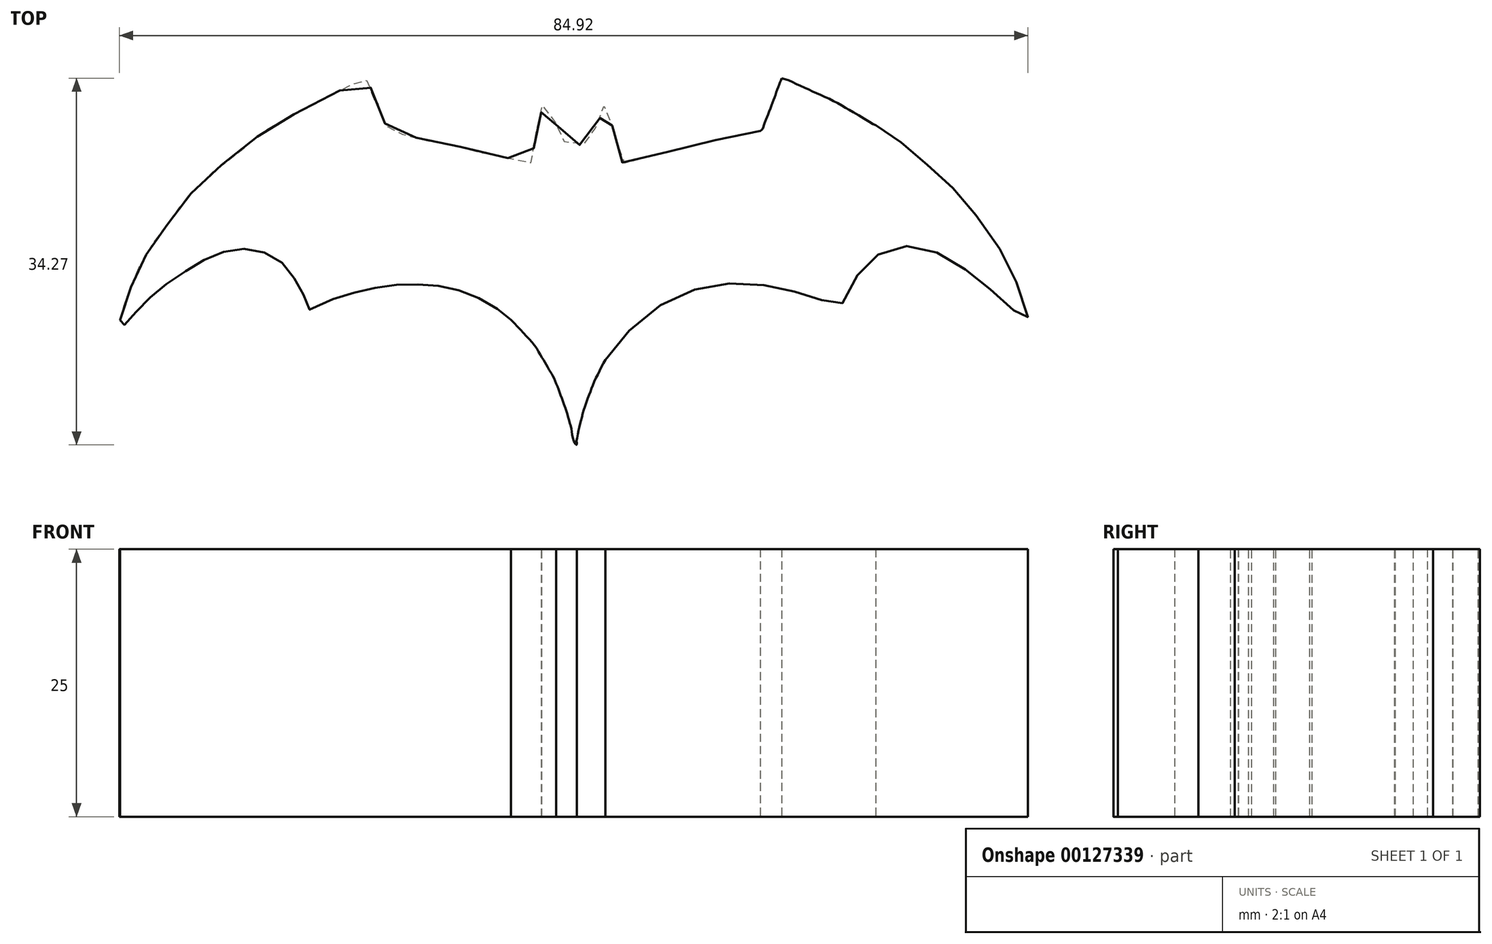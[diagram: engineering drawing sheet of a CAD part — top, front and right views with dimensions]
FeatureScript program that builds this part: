
annotation { "Feature Type Name" : "Feature", "Feature Type Description" : "" }
export const myFeature = defineFeature(function(context is Context, id is Id, definition is map)
    precondition{}
    {
        {
            var Q0;
            Q0=qCreatedBy(makeId("Top.planeOp"),FACE);
            var sketch = newSketch(context, id + "F0", { "sketchPlane" : qUnion([Q0])});
            skFitSpline(sketch, "E0", {"points": [v(-40.2, -23.09) * mm, v(-39.85, -21.8) * mm, v(-39.51, -20.78) * mm, v(-39, -19.58) * mm, v(-38.57, -18.47) * mm, v(-37.89, -17.2) * mm, v(-37.29, -16.17) * mm, v(-36.52, -15.14) * mm, v(-35.58, -13.86) * mm, v(-34.73, -12.66) * mm, v(-33.7, -11.38) * mm, v(-32.59, -10.27) * mm, v(-31.22, -8.99) * mm, v(-29.5, -7.7) * mm, v(-27.89, -6.34) * mm, v(-26.43, -5.23) * mm, v(-24.9, -4.37) * mm, v(-22.76, -3.18) * mm, v(-20.2, -1.9) * mm, v(-18.3, -0.95) * mm, v(-17.11, -0.7) * mm, v(-16.69, -1.64) * mm, v(-16.09, -3) * mm, v(-15.49, -4.46) * mm, v(-15.23, -5.31) * mm, v(-13.7, -5.74) * mm, v(-12.07, -6.17) * mm, v(-9.85, -6.6) * mm, v(-7.88, -7.02) * mm, v(-5.57, -7.62) * mm, v(-3.18, -8.13) * mm, v(-1.8, -8.39) * mm, v(-1.55, -7.2) * mm, v(-1.38, -5.91) * mm, v(-1.04, -4.37) * mm, v(-0.78, -3.35) * mm, v(-0.78, -3) * mm, v(0, -3.69) * mm, v(0.67, -5.14) * mm, v(1.18, -6.25) * mm, v(2.12, -6.68) * mm, v(3.4, -6.5) * mm, v(4, -5.57) * mm, v(4.6, -4.37) * mm, v(5.12, -3) * mm, v(5.54, -4.2) * mm, v(5.89, -5.14) * mm, v(6.31, -6.94) * mm, v(6.66, -8.3) * mm, v(8.62, -7.96) * mm, v(10.67, -7.45) * mm, v(13.24, -6.76) * mm, v(15.55, -6.25) * mm, v(18.03, -5.74) * mm, v(19.65, -5.4) * mm], "startDerivative": vector(20.17, 77.9) * mm, "endDerivative": vector(79.85, 16.89) * mm});
            skFitSpline(sketch, "E1", {"points": [v(19.65, -5.4) * mm, v(19.87, -5.18) * mm, v(20.05, -4.64) * mm, v(20.25, -4.14) * mm, v(20.71, -3) * mm, v(21.06, -2.04) * mm, v(21.4, -1.1) * mm, v(21.65, -0.47) * mm], "startDerivative": vector(2.6, 1.9) * mm, "endDerivative": vector(1.8, 4.32) * mm});
            skFitSpline(sketch, "E2", {"points": [v(21.65, -0.47) * mm, v(22.28, -0.66) * mm, v(23.01, -1.02) * mm, v(23.95, -1.43) * mm, v(24.76, -1.8) * mm, v(25.67, -2.21) * mm, v(26.64, -2.67) * mm, v(27.55, -3.2) * mm, v(28.4, -3.68) * mm, v(29.95, -4.62) * mm, v(30.43, -4.87) * mm], "startDerivative": vector(7.62, -2.01) * mm, "endDerivative": vector(5.28, -2.55) * mm});
            skFitSpline(sketch, "E3", {"points": [v(30.43, -4.87) * mm, v(31.3, -5.56) * mm, v(32.41, -6.18) * mm, v(33.66, -7.15) * mm, v(34.83, -8.19) * mm, v(35.87, -9.09) * mm, v(37.05, -10.06) * mm, v(38.15, -11.3) * mm, v(39.26, -12.48) * mm, v(40.3, -14) * mm, v(41.68, -15.87) * mm, v(42.58, -17.46) * mm, v(43.41, -19.12) * mm, v(44.04, -20.78) * mm, v(44.59, -22.37) * mm, v(44.59, -23.4) * mm, v(44.1, -22.86) * mm, v(43.34, -22.16) * mm, v(42.58, -21.4) * mm, v(41.4, -20.43) * mm, v(40.58, -19.67) * mm, v(39.54, -18.84) * mm, v(38.3, -18.01) * mm, v(36.98, -17.25) * mm, v(35.87, -16.63) * mm, v(34.49, -16.28) * mm, v(33.45, -16.15) * mm, v(32.14, -16.35) * mm, v(30.96, -16.7) * mm, v(30.43, -17.18) * mm, v(29.65, -17.88) * mm, v(28.75, -18.84) * mm, v(27.92, -20.23) * mm, v(27.43, -21.13) * mm, v(27.16, -21.82) * mm, v(26.53, -21.54) * mm, v(25.7, -21.33) * mm, v(24.73, -20.92) * mm, v(23.83, -20.64) * mm, v(22.66, -20.37) * mm, v(21.48, -20.09) * mm, v(20.24, -19.88) * mm, v(18.92, -19.6) * mm, v(17.26, -19.6) * mm, v(15.46, -19.81) * mm, v(13.94, -20.09) * mm, v(12.49, -20.64) * mm, v(10.7, -21.47) * mm, v(9.1, -22.44) * mm, v(7.44, -24.03) * mm, v(5.85, -25.9) * mm, v(5.16, -26.8) * mm], "startDerivative": vector(47.12, -41.42) * mm, "endDerivative": vector(-34.24, -45.67) * mm});
            skPoint(sketch, "E4.4.internal.snap0", {"position": v(2.3, -35.37) * mm});
            skFitSpline(sketch, "E5", {"points": [v(5.16, -26.8) * mm, v(4.8, -27.45) * mm, v(4.46, -28.16) * mm, v(4.12, -28.84) * mm, v(3.9, -29.43) * mm, v(3.69, -29.93) * mm, v(3.46, -30.53) * mm, v(3.2, -31.3) * mm, v(3.03, -31.92) * mm, v(2.87, -32.53) * mm, v(2.73, -33.05) * mm, v(2.64, -33.49) * mm, v(2.5, -34.17) * mm, v(2.46, -34.4) * mm], "startDerivative": vector(-4.26, -7.58) * mm, "endDerivative": vector(-0.8, -3.99) * mm});
            skFitSpline(sketch, "E6", {"points": [v(2.47, -34.34) * mm, v(2.46, -34.74) * mm, v(2.14, -34.17) * mm, v(2, -33.35) * mm, v(1.8, -32.53) * mm, v(1.55, -31.68) * mm, v(1.2, -30.7) * mm, v(0.89, -29.8) * mm, v(0.57, -29.03) * mm], "startDerivative": vector(0.6, -6.74) * mm, "endDerivative": vector(-2.52, 5.88) * mm});
            skFitSpline(sketch, "E7", {"points": [v(0.57, -29.03) * mm, v(0.26, -28.3) * mm, v(0, -27.88) * mm, v(-0.37, -27.21) * mm, v(-0.75, -26.59) * mm, v(-1.34, -25.61) * mm, v(-2.36, -24.42) * mm, v(-3.65, -23.07) * mm], "startDerivative": vector(-2.45, 6.3) * mm, "endDerivative": vector(-6.73, 7.06) * mm});
            skFitSpline(sketch, "E8", {"points": [v(-3.65, -23.07) * mm, v(-4.7, -22.2) * mm, v(-6.4, -21.15) * mm, v(-8.3, -20.36) * mm, v(-10.2, -19.9) * mm, v(-12.1, -19.77) * mm, v(-14.08, -19.77) * mm, v(-16.17, -20.03) * mm, v(-18.14, -20.5) * mm, v(-20.24, -21.08) * mm, v(-22.67, -22.07) * mm, v(-23.06, -20.76) * mm, v(-23.78, -19.38) * mm, v(-24.83, -17.94) * mm, v(-26.27, -16.95) * mm, v(-28.18, -16.43) * mm, v(-30.01, -16.56) * mm, v(-31.98, -17.28) * mm, v(-33.68, -18.26) * mm, v(-35.72, -19.58) * mm, v(-37.23, -20.82) * mm, v(-38.6, -22.2) * mm, v(-39.39, -23.09) * mm, v(-40.2, -23.77) * mm, v(-40.2, -23.09) * mm], "startDerivative": vector(-26.82, 23.56) * mm, "endDerivative": vector(6.3, 37.96) * mm});
            skSolve(sketch);
        }
        {
            var Q0;
            Q0=makeQuery(id+"F0.imprint","IMPRINT",FACE,{"disambiguationData":[TD([[makeQuery(id+"F0.imprint","IMPRINT",EDGE,{"derivedFrom":sQuery(id+"F0.wireOp",EDGE,"E0")}),-1.0]])]});
            extrude(context, id + "F1", {"entities" : qUnion([Q0]), "depth" : 25 * mm});
        }
    });
